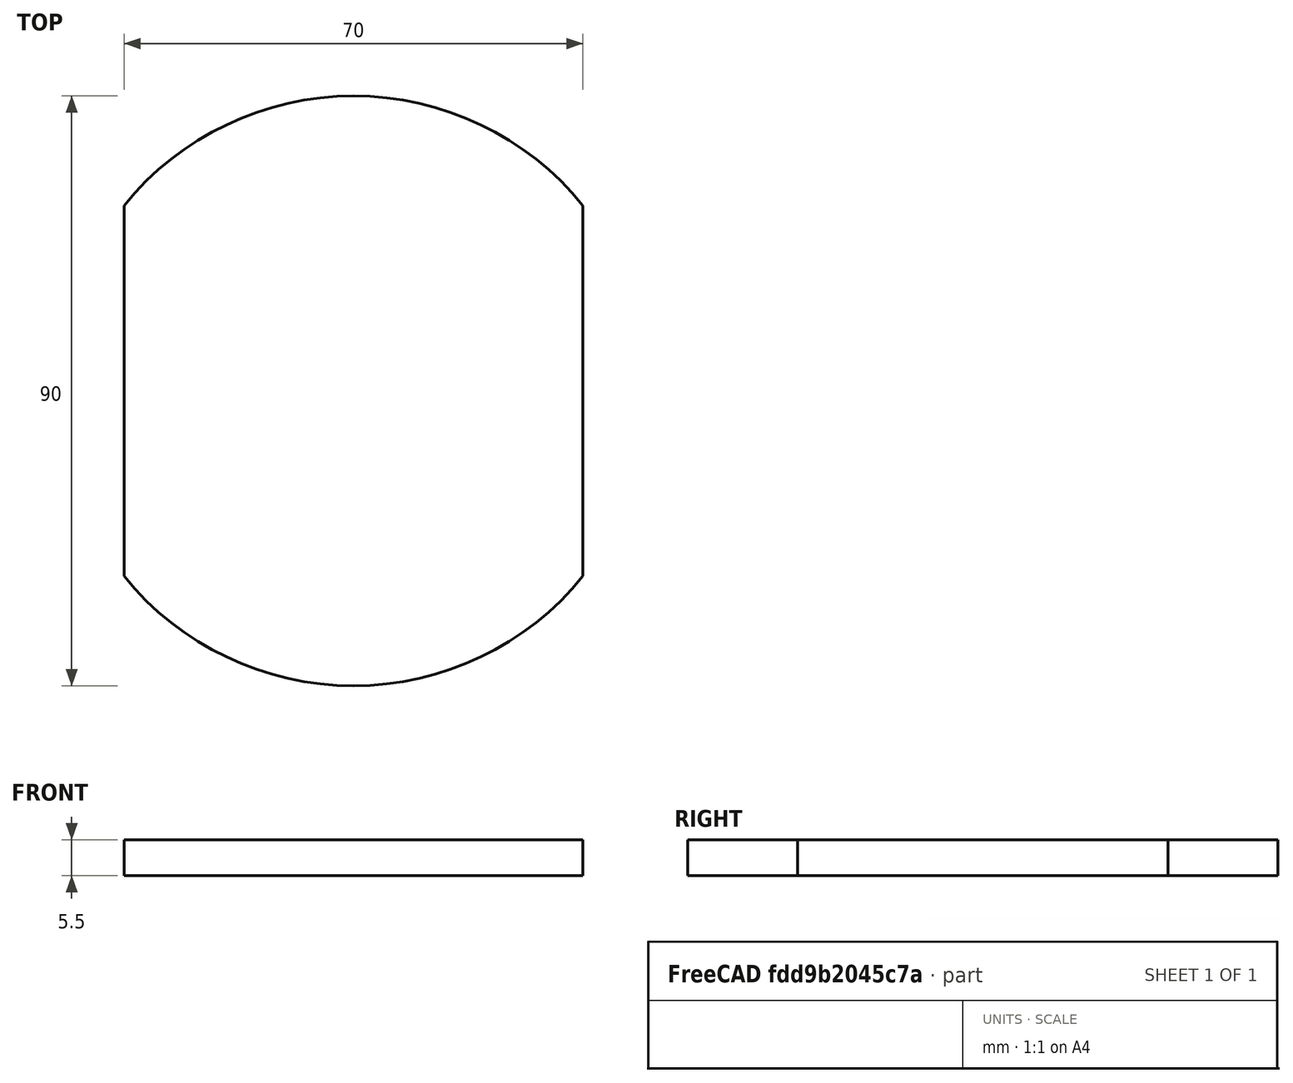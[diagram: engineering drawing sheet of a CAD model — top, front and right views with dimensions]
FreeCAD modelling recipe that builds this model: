
FCSTD DOCUMENT  (FreeCAD 1.0R39319 (Git))
Label: chapa_circle_90mm
License: All rights reserved
LicenseURL: https://en.wikipedia.org/wiki/All_rights_reserved
objects: Sketcher::SketchObject×3, PartDesign::Pocket×2, PartDesign::Pad×1, PartDesign::Body×1
note: 16 computed .brp shape members not serialized (recipe doc carries the construction recipe); baked Part::Feature solids carry a one-line shape summary decoded from their .brp

FEATURE [Sketcher::SketchObject] Sketch_1
  ArcFitTolerance = 1e-06
  AttachmentSupport = -> [XY_Plane]
  FullyConstrained = false
  MakeInternals = false
  MapMode = 5
  sketch-geometry (1):
    g0: Circle CenterX=0 CenterY=0 CenterZ=0 NormalX=0 NormalY=0 NormalZ=1 AngleXU=0 Radius=45
FEATURE [PartDesign::Pad] Pad_1
  Direction = (0,0,1)
  Length = 5.5
  Length2 = 10
  Profile = -> Sketch_1
  Refine = true
  Suppressed = false
  Type = 0
FEATURE [Sketcher::SketchObject] Sketch_2
  ArcFitTolerance = 1e-06
  AttachmentSupport = -> [Pad_1]
  FullyConstrained = false
  MakeInternals = false
  MapMode = 5
  Placement = pos=(0,0,5.5) rot=(0,0,1;0rad)
  sketch-geometry (4):
    g0: LineSegment StartX=-50 StartY=-50 StartZ=0 EndX=-35 EndY=-50 EndZ=0
    g1: LineSegment StartX=-35 StartY=-50 StartZ=0 EndX=-35 EndY=50 EndZ=0
    g2: LineSegment StartX=-35 StartY=50 StartZ=0 EndX=-50 EndY=50 EndZ=0
    g3: LineSegment StartX=-50 StartY=50 StartZ=0 EndX=-50 EndY=-50 EndZ=0
  constraints (4):
    c: Coincident(g0,g1)
    c: Coincident(g1,g2)
    c: Coincident(g2,g3)
    c: Coincident(g3,g0)
FEATURE [PartDesign::Pocket] Pocket_2
  BaseFeature = -> Pad_1
  Direction = (0,0,-1)
  Length = 5
  Length2 = 5
  Profile = -> Sketch_2
  Refine = true
  Suppressed = false
  Type = 1
FEATURE [Sketcher::SketchObject] Sketch_3
  ArcFitTolerance = 1e-06
  AttachmentSupport = -> [Pocket_2]
  FullyConstrained = false
  MakeInternals = false
  MapMode = 5
  Placement = pos=(0,0,5.5) rot=(0,0,1;0rad)
  sketch-geometry (4):
    g0: LineSegment StartX=35 StartY=-50 StartZ=0 EndX=50 EndY=-50 EndZ=0
    g1: LineSegment StartX=50 StartY=-50 StartZ=0 EndX=50 EndY=50 EndZ=0
    g2: LineSegment StartX=50 StartY=50 StartZ=0 EndX=35 EndY=50 EndZ=0
    g3: LineSegment StartX=35 StartY=50 StartZ=0 EndX=35 EndY=-50 EndZ=0
  constraints (4):
    c: Coincident(g0,g1)
    c: Coincident(g1,g2)
    c: Coincident(g2,g3)
    c: Coincident(g3,g0)
FEATURE [PartDesign::Pocket] Pocket_3
  BaseFeature = -> Pocket_2
  Direction = (0,0,-1)
  Length = 5
  Length2 = 5
  Profile = -> Sketch_3
  Refine = true
  Suppressed = false
  Type = 1
FEATURE [PartDesign::Body] Body
  AllowCompound = false
  Group = -> [Sketch_1,Pad_1,Sketch_2,Pocket_2,Sketch_3,Pocket_3]
  Origin = -> Origin
  Tip = -> Pocket_3
